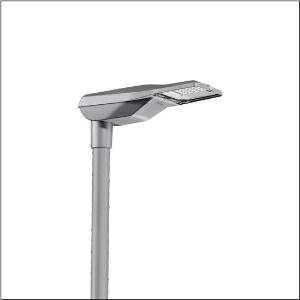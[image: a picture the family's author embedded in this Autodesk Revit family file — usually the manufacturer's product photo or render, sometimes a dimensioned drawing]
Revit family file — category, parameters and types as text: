
# Revit family: streetlight_sl_21_iq_micro___stw1_0a_5xe1e41g08db_19ca
name_source: partatom
category: Lighting Fixtures
units: mm (PartAtom-declared; Revit-internal decimal feet)

## family parameters
Cut with Voids When Loaded = No
Host = Face
Light Source = No
Part Type = Normal
Room Calculation Point = No
Round Connector Dimension = Use Diameter
Shared = No

## types (1)
- --- (1 x LED, 5010 lm, 36.4 W, 4000K)
    Apparent Load = 36 VA
    CIE Flux Codes = 38 75 98 100 100
    Color Rendering = 70
    Color Temperature = 4000K
    Default Elevation = 1800 mm
    Description = Streetlight SL 21 iQ micro, mast luminaire, primary light control with lens, of PMMA, primary optical cover: cover, of toughened safety glass, transparent, light distribution: STW1.0a, light emission: direct distribution, primary light characteristic: asymmetric, installation type: post-top, side-entry, LED, High Power LED, rated luminous flux: 5.010lm, luminous efficacy: 138lm/W, light colour: 740, colour temperature: 4000K, control: Street-Remote, Auto-Match, Temp-Guard, Lumen-Switch, Night-Set, Smart-Wire, Light-Fading, Desk-Remote (wireless, voltage-free reading and setting of iQ features in the workshop via application-optimized NFC function/RFID function), optimised constant luminous flux control (CLO 2.0), presetting dimming linear, mains connection: 220..240V, AC, 50/60Hz, start of lifetime: 36W, end of service life: 38W, reduction: 16W, luminaire housing, of diecast aluminium, powder-coated, Siteco® metallic grey (DB 702S), corrosivity category C5 mid according to DIN EN ISO 12944, please order mast flange separately, inclination adjustable: 0°, 5°, 10°, 15°, sealing non-destructively replaceable, multi-level sealing system, length: 528mm, width: 235mm, height: 110mm, mast flange for spigot size: 42mm (side-entry): 5XC10008XM4, 60/48mm (side-entry/post-top): 5XC10108XM2, 76/60mm (side-entry/post-top): 5XC10108XM1, protection rating (complete): IP66, insulation class (complete): insulation class II (safety insulation), certification: CE, ENEC, ENEC+, VDE, impact resistance: IK09, permissible operating ambient temperature for outdoor applications: -40..+50°C, standard-compliant lighting for roads and squares, packaging unit: 1 piece

Light Distribution: STW1.0a
    Height = 110 mm
    Lamp = 1 x LED
    Lamp Light Flux = 5010 lm
    Lamp Power = 36.4 W
    Lamp count = 1
    Length = 528 mm
    Luminous efficacy = 138 lm/W
    Manufacturer = Siteco
    ModVariant = No
    Model = 5XE1E41G08DB
    Number of Poles = 1
    OnlyDefault = Yes
    Power Factor = 1
    Product Name = Streetlight SL 21 iQ micro | STW1.0a
    Product group = mast luminaire | pylon top
    ProductGroupID = 6100
    Protection Class = Protection class II
    Protection Degree = IP 66
    RLX_Detail_Level = 1
    RLX_Emergency_Light_Flux = 0 lm
    RLX_Emergency_Type = 0
    RLX_Emergency_Type_DB = No
    RlxData = <blob elided: 99325 chars, md5=38ef4602>
    Socket = socket
    Standby Power = 0 W
    System Light Flux = 5010 lm
    System Power = 36 W
    Type Comments = factory setting: luminous flux: 100 % | dim-lin: 254 | 715 mA
    Type Image = l_1006881.jpg
    URL = http://relux.com
    VarID = @adj_087689
    Voltage = 0 V
    Weight = 0.00 kg
    Width = 235 mm

## geometry (parser evidence)
native form markers: Blend x4, Sweep x11
no freeform markers — native parametric forms only
